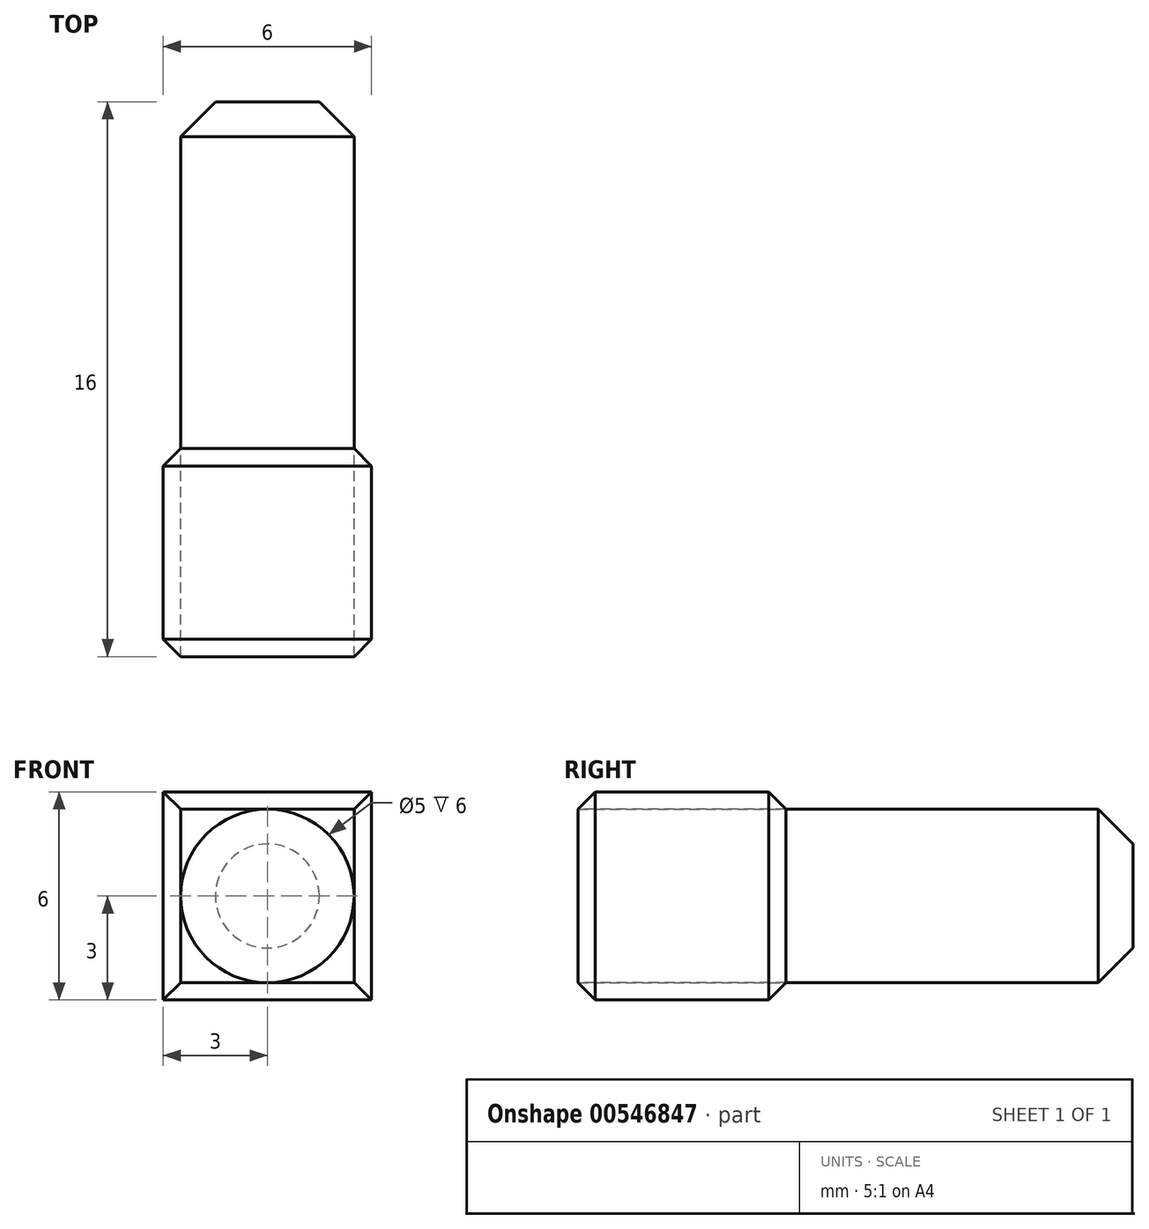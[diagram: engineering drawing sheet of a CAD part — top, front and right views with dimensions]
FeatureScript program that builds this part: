
annotation { "Feature Type Name" : "Feature", "Feature Type Description" : "" }
export const myFeature = defineFeature(function(context is Context, id is Id, definition is map)
    precondition{}
    {
        {
            var Q0;
            Q0=qCreatedBy(makeId("Front.planeOp"),FACE);
            var sketch = newSketch(context, id + "F0", { "sketchPlane" : qUnion([Q0])});
            skCircle(sketch, "E0", {"center": v(0, 0) * mm, "radius": 2.5 * mm});
            skCircle(sketch, "E1.cCircle", {"center": v(0, 0) * mm, "radius": 3 * mm, "construction": true});
            skLineSegment(sketch, "E1.0", {"start": v(-3, 3) * mm, "end": v(3, 3) * mm});
            skLineSegment(sketch, "E1.1", {"start": v(3, 3) * mm, "end": v(3, -3) * mm});
            skLineSegment(sketch, "E1.2", {"start": v(3, -3) * mm, "end": v(-3, -3) * mm});
            skLineSegment(sketch, "E1.3", {"start": v(-3, -3) * mm, "end": v(-3, 3) * mm});
            skPoint(sketch, "E1.0.midPoint", {"position": v(0, 3) * mm});
            skSolve(sketch);
        }
        {
            var Q0;
            Q0=makeQuery(id+"F0.imprint","IMPRINT",FACE,{"disambiguationData":[TD([[makeQuery(id+"F0.imprint","IMPRINT",EDGE,{"derivedFrom":sQuery(id+"F0.wireOp",EDGE,"E0")}),1.0]])]});
            extrude(context, id + "F1", {"entities" : qUnion([Q0]), "oppositeDirection" : true, "depth" : 10 * mm, "offsetDistance" : 25 * mm, "hasSecondDirection" : true, "secondDirectionOppositeDirection" : false, "secondDirectionDepth" : 6 * mm});
        }
        {
            var Q0;
            Q0=makeQuery(id+"F1.opExtrude","CAP_EDGE",EDGE,{"disambiguationData":[OSD([sQuery(id+"F0.wireOp",EDGE,"E0")])],"isStart":false});
            chamfer(context, id + "F2", {"entities" : qUnion([Q0]), "width" : 1 * mm, "tangentPropagation" : true});
        }
        {
            var Q0;
            Q0=makeQuery(id+"F0.imprint","IMPRINT",FACE,{"disambiguationData":[TD([[makeQuery(id+"F0.imprint","IMPRINT",EDGE,{"derivedFrom":sQuery(id+"F0.wireOp",EDGE,"E0")}),-1.0]])]});
            extrude(context, id + "F3", {"entities" : qUnion([Q0]), "depth" : 6 * mm, "offsetDistance" : 25 * mm});
        }
        {
            var Q0;
            Q0=makeQuery(id+"F3.opExtrude","CAP_EDGE",EDGE,{"disambiguationData":[OSD([sQuery(id+"F0.wireOp",EDGE,"E1.1")])],"isStart":false});
            var Q1;
            Q1=makeQuery(id+"F3.opExtrude","CAP_EDGE",EDGE,{"disambiguationData":[OSD([sQuery(id+"F0.wireOp",EDGE,"E1.0")])],"isStart":false});
            var Q2;
            Q2=makeQuery(id+"F3.opExtrude","CAP_EDGE",EDGE,{"disambiguationData":[OSD([sQuery(id+"F0.wireOp",EDGE,"E1.3")])],"isStart":false});
            var Q3;
            Q3=makeQuery(id+"F3.opExtrude","CAP_EDGE",EDGE,{"disambiguationData":[OSD([sQuery(id+"F0.wireOp",EDGE,"E1.2")])],"isStart":false});
            var Q4;
            Q4=makeQuery(id+"F3.opExtrude","CAP_EDGE",EDGE,{"disambiguationData":[OSD([sQuery(id+"F0.wireOp",EDGE,"E1.1")])],"isStart":true});
            var Q5;
            Q5=makeQuery(id+"F3.opExtrude","CAP_EDGE",EDGE,{"disambiguationData":[OSD([sQuery(id+"F0.wireOp",EDGE,"E1.3")])],"isStart":true});
            var Q6;
            Q6=makeQuery(id+"F3.opExtrude","CAP_EDGE",EDGE,{"disambiguationData":[OSD([sQuery(id+"F0.wireOp",EDGE,"E1.0")])],"isStart":true});
            var Q7;
            Q7=makeQuery(id+"F3.opExtrude","CAP_EDGE",EDGE,{"disambiguationData":[OSD([sQuery(id+"F0.wireOp",EDGE,"E1.2")])],"isStart":true});
            chamfer(context, id + "F4", {"entities" : qUnion([Q0, Q1, Q2, Q3, Q4, Q5, Q6, Q7]), "width" : .5 * mm, "tangentPropagation" : true});
        }
    });
